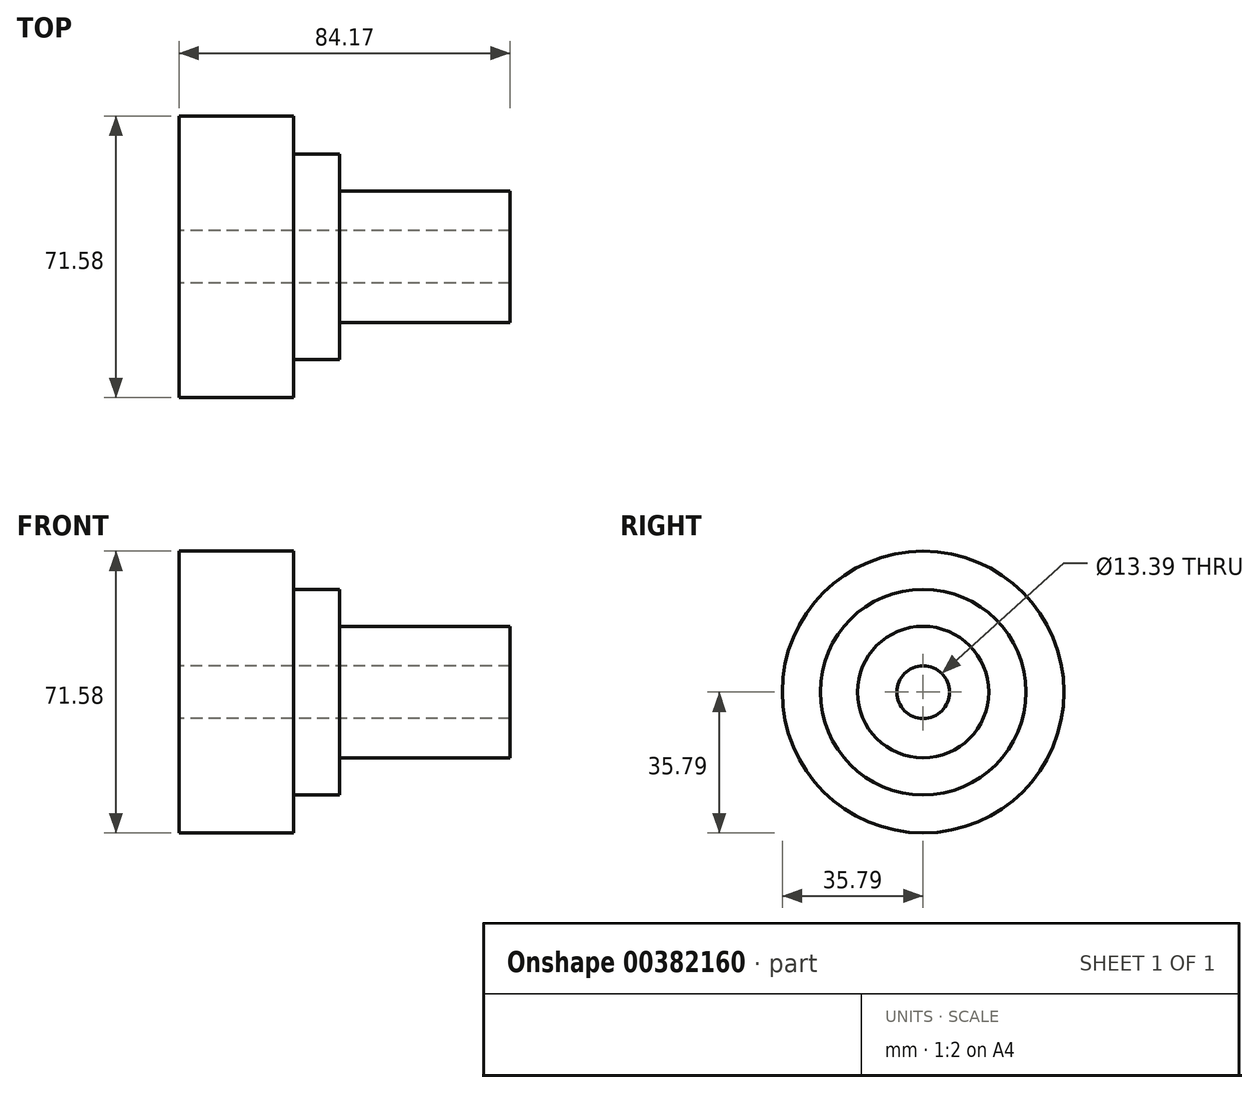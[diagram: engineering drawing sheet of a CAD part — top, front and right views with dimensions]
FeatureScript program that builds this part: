
annotation { "Feature Type Name" : "Feature", "Feature Type Description" : "" }
export const myFeature = defineFeature(function(context is Context, id is Id, definition is map)
    precondition{}
    {
        {
            var Q0;
            Q0=qCreatedBy(makeId("Front.planeOp"),FACE);
            var sketch = newSketch(context, id + "F0", { "sketchPlane" : qUnion([Q0])});
            skLineSegment(sketch, "E0", {"start": v(-71.57, 0) * mm, "end": v(69.26, 0) * mm, "construction": true});
            skLineSegment(sketch, "E1.bottom", {"start": v(-71.32, 6.7) * mm, "end": v(-42.22, 6.7) * mm});
            skLineSegment(sketch, "E1.top", {"start": v(-71.32, 35.79) * mm, "end": v(-42.22, 35.79) * mm});
            skLineSegment(sketch, "E1.left", {"start": v(-71.32, 6.7) * mm, "end": v(-71.32, 35.79) * mm});
            skLineSegment(sketch, "E1.right", {"start": v(-42.22, 6.7) * mm, "end": v(-42.22, 35.79) * mm});
            skLineSegment(sketch, "E2.bottom", {"start": v(-49.89, 6.7) * mm, "end": v(-30.45, 6.7) * mm});
            skLineSegment(sketch, "E2.top", {"start": v(-49.89, 26.13) * mm, "end": v(-30.45, 26.13) * mm});
            skLineSegment(sketch, "E2.left", {"start": v(-49.89, 6.7) * mm, "end": v(-49.89, 26.13) * mm});
            skLineSegment(sketch, "E2.right", {"start": v(-30.45, 6.7) * mm, "end": v(-30.45, 26.13) * mm});
            skLineSegment(sketch, "E3.bottom", {"start": v(-37.15, 6.7) * mm, "end": v(12.85, 6.7) * mm});
            skLineSegment(sketch, "E3.top", {"start": v(-37.15, 16.7) * mm, "end": v(12.85, 16.7) * mm});
            skLineSegment(sketch, "E3.left", {"start": v(-37.15, 6.7) * mm, "end": v(-37.15, 16.7) * mm});
            skLineSegment(sketch, "E3.right", {"start": v(12.85, 6.7) * mm, "end": v(12.85, 16.7) * mm});
            skSolve(sketch);
        }
        {
            var Q0;
            Q0 = qSketchRegion(id + "F0", true);
            var Q1;
            Q1=sQuery(id+"F0.wireOp",EDGE,"E0");
            revolve(context, id + "F1", {"entities" : qUnion([Q0]), "axis" : qUnion([Q1]), "revolveType" : RevolveType.FULL});
        }
    });
